# Revit family: Storage-Freestanding-Teknion-BSUS_Storage_Unit_Solid_Doors-R2019
name_source: partatom
category: Furniture
units: mm (PartAtom-declared; Revit-internal decimal feet)

## family parameters
Always vertical = Yes
Cut with Voids When Loaded = No
OmniClass Number = 23.40.20.00
OmniClass Title = General Furniture and Specialties
Room Calculation Point = No
Shared = Yes
Work Plane-Based = No

## types (3) — shared parameters
Assembly Code = E2020200
Manufacturer = Teknion
Manufacturer Fax = 416.661.4586
Part Number = BSUS
Product Documentation Link = https://www.teknion.com
Product Line = Expansion Casegoods
Product Page URL = https://www.teknion.com
Series = Expansion Casegoods
Sustainability Data = https://www.teknion.com
URL = www.teknion.com
Unit Weight URL = http://www.teknion.com
Warranty = http://www.teknion.com

## per-type parameters (varying)
| type | Depth | Description | Model |
| 24" Depth | 24 " | Storage Unit - Open Shelves, 24" Depth | BSUS_24____ |
| 20" Depth | 20 " | Storage Unit - Open Shelves, 20" Depth | BSUS_20____ |
| 18" Depth | 18 " | Storage Unit - Open Shelves, 18" Depth | BSUS_18____ |

## geometry (parser evidence)
native form markers: Sweep x3
no freeform markers — native parametric forms only
